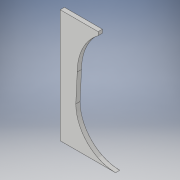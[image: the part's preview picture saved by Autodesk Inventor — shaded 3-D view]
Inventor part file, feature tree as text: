
AUTODESK INVENTOR PART (.ipt)
format: ipt  version: 2018 (Build 220112000, 112)  size: 155,136 bytes
history: native  units: in
note: dims shown in document units (in); Inventor stores cm internally (conversion verified against a paired STEP export)
features: extrude x1, direct_edit x1, sketch x1, move_body x1
ambient origin geometry x8: Origin, YZ Plane, XZ Plane, XY Plane, X Axis, Y Axis, Z Axis, Center Point
bodies: Body1 (feature_tree)
feature tree (4):
  extrude  "Extrusion2"  Depth=0.75in
  direct_edit  "Direct Edit1"
  sketch  "Sketch1"  dims[d0=24.0in d1=8.25in d2=12.0in d3=6.5in d4=6.5in d5=12.0in d6=7.0in d7=7.0in d8=1.0in d9=0.5in d10=135.0deg d11=6.5in d12=135.0deg d13=6.5in d14=7.0in d15=0.625in d16=1.0in d17=5.0in d20=5.0in d21=3.0in d22=6.0in d23=1.0in d24=2.0in d26=0.8727in d33=6.25in d34=0.8727in d35=1.0994in d36=6.25in d37=180.0deg d45=150.0deg d46=6.25in d47=180.0deg d72=26.0in d73=20.0in d74=90.0deg d75=0.75in d76=0.0in d77=5.9332in d78=0.6126in d83=0.0in d84=0.0in d85=0.75in]
  move_body  "Move1"
